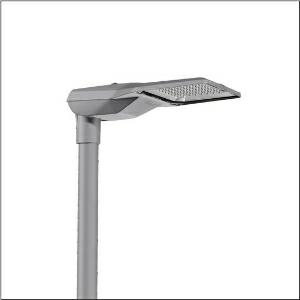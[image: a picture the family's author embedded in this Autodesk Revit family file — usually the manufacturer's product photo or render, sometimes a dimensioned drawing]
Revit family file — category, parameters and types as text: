
# Revit family: streetlight_sl_21_midi___pl52_5xe3h33s08lb_2890
name_source: partatom
category: Lighting Fixtures
units: mm (PartAtom-declared; Revit-internal decimal feet)

## family parameters
Cut with Voids When Loaded = No
Host = Face
Light Source = No
Part Type = Normal
Room Calculation Point = No
Round Connector Dimension = Use Diameter
Shared = No

## types (1)
- --- (1 x LED, 14100 lm, 99.6 W, 3000K)
    Apparent Load = 100 VA
    CIE Flux Codes = 27 59 98 100 100
    Color Rendering = 70
    Color Temperature = 3000K
    Default Elevation = 1800 mm
    Description = Streetlight SL 21 midi, mast luminaire, primary light control with lens, of PMMA, primary optical cover: cover, of toughened safety glass, transparent, light distribution: PL52, light emission: direct distribution, primary light characteristic: asymmetric, installation type: side-entry, post-top, LED, High Power LED, rated luminous flux: 14.100lm, luminous efficacy: 142lm/W, light colour: 730, colour temperature: 3000K, control gear: D4i, control: overheat protection, constant luminous flux control, time-dependent luminous flux control, flexible luminous flux parameterisation, pre-setting: logarithmic dimming characteristic, mains connection: 230..240V, AC, 50/60Hz, start of lifetime: 100W, end of service life: 102W, reduction: 46W, luminaire housing, of diecast aluminium, powder-coated, Siteco® metallic grey (DB 702S), corrosivity category C5 mid according to DIN EN ISO 12944, please order mast flange separately, inclination adjustable: 0°, 5°, 10°, 15°, sealing non-destructively replaceable, multi-level sealing system, length: 644mm, width: 335mm, height: 110mm, mast flange for spigot size: 42mm (side-entry): 5XC10008XM4, 60/48mm (side-entry/post-top): 5XC10108XM2, 76/60mm (side-entry/post-top): 5XC10108XM1, mounting height: 4..8m, Smart Interface above, protection rating (complete): IP66, insulation class (complete): insulation class II (safety insulation), certification: CE, ENEC, ENEC+, VDE, impact resistance: IK10, permissible operating ambient temperature for outdoor applications: -40..+50°C, standard-compliant lighting for roads and squares, packaging unit: 1 piece

Light Distribution: PL52
    Height = 111 mm
    Lamp = 1 x LED
    Lamp Light Flux = 14100 lm
    Lamp Power = 99.6 W
    Lamp count = 1
    Length = 644 mm
    Luminous efficacy = 142 lm/W
    Manufacturer = Siteco
    ModVariant = No
    Model = 5XE3H33S08LB
    Number of Poles = 1
    OnlyDefault = Yes
    Power Factor = 1
    Product Name = Streetlight SL 21 midi | PL52
    Product group = mast luminaire | pylon top
    ProductGroupID = 6100
    Protection Class = Protection class II
    Protection Degree = IP 66
    RLX_Detail_Level = 1
    RLX_Emergency_Light_Flux = 0 lm
    RLX_Emergency_Type = 0
    RLX_Emergency_Type_DB = No
    RlxData = <blob elided: 36409 chars, md5=62d4ea7c>
    Socket = socket
    Standby Power = 0 W
    System Light Flux = 14100 lm
    System Power = 100 W
    Type Comments = factory setting: luminous flux: 100 % | dim-lin: 254 | 1020 mA
    Type Image = l_1004302.jpg
    URL = http://relux.com
    VarID = @adj_032427
    Voltage = 0 V
    Weight = 0.00 kg
    Width = 336 mm

## geometry (parser evidence)
native form markers: Blend x4, Sweep x9
no freeform markers — native parametric forms only
